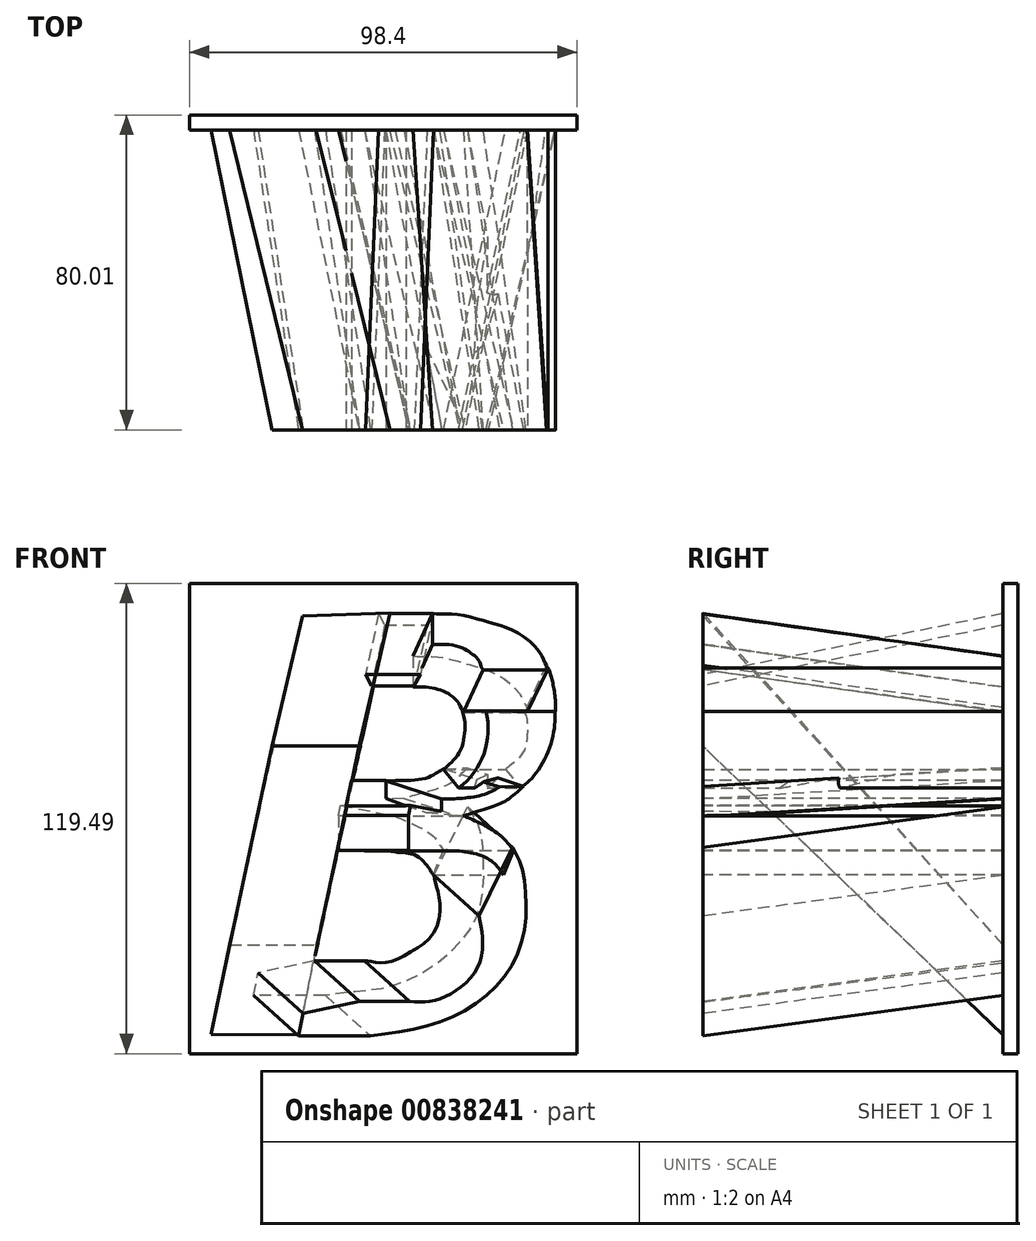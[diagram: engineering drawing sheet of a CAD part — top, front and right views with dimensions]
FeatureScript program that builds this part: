
annotation { "Feature Type Name" : "Feature", "Feature Type Description" : "" }
export const myFeature = defineFeature(function(context is Context, id is Id, definition is map)
    precondition{}
    {
        {
            var Q0;
            Q0=qCreatedBy(makeId("Front.planeOp"),FACE);
            var sketch = newSketch(context, id + "F0", { "sketchPlane" : qUnion([Q0])});
            skText(sketch, "E0", { "text": "B 3 D", "fontName": "OpenSans-BoldItalic.ttf"});
            const initialGuessF0  = {"E0": [-0.06398, -0.05174, 1, 0, 0.10807]};
            skSetInitialGuess(sketch, initialGuessF0);
            skSolve(sketch);
        }
        {
            var Q0;
            Q0 = qSketchRegion(id + "F0", true);
            var sketch = newSketch(context, id + "F1", { "sketchPlane" : qUnion([Q0])});
            skLineSegment(sketch, "E1", {"start": v(-36.57, 54.73) * mm, "end": v(-44.32, 21.63) * mm});
            skLineSegment(sketch, "E2", {"start": v(-44.32, 21.63) * mm, "end": v(-22.25, 21.63) * mm});
            skLineSegment(sketch, "E3", {"start": v(-22.25, 21.63) * mm, "end": v(-14.38, 55.5) * mm});
            skLineSegment(sketch, "E4", {"start": v(-14.38, 55.5) * mm, "end": v(-36.57, 54.73) * mm});
            skSolve(sketch);
        }
        {
            var Q0;
            Q0=qCreatedBy(makeId("Front.planeOp"),FACE);
            cPlane(context, id + "F2", {"entities" : qUnion([Q0]), "cplaneType" : CPlaneType.OFFSET, "offset" : 76.2 * mm, "oppositeDirection" : true, "width" : 152.4 * mm, "height" : 152.4 * mm});
        }
        {
            var Q0;
            Q0=qCreatedBy(id+"F2.planeOp",FACE);
            var sketch = newSketch(context, id + "F3", { "sketchPlane" : qUnion([Q0])});
            skLineSegment(sketch, "E5", {"start": v(-59.85, -51.56) * mm, "end": v(-55.1, -28.85) * mm});
            skLineSegment(sketch, "E6", {"start": v(-55.1, -28.85) * mm, "end": v(-33.1, -28.85) * mm});
            skLineSegment(sketch, "E7", {"start": v(-33.1, -28.85) * mm, "end": v(-37.58, -51.71) * mm});
            skLineSegment(sketch, "E8", {"start": v(-37.58, -51.71) * mm, "end": v(-59.85, -51.56) * mm});
            skSolve(sketch);
        }
        {
            var Q0;
            Q0 = qSketchRegion(id + "F3", true);
            var Q1;
            Q1 = qSketchRegion(id + "F1", true);
            loft(context, id + "F4", {"sheetProfilesArray" : [{ "sheetProfileEntities" : qUnion([Q0]) }, { "sheetProfileEntities" : qUnion([Q1]) }]});
        }
        {
            var Q0;
            Q0=qCreatedBy(id+"F2.planeOp",FACE);
            var sketch = newSketch(context, id + "F5", { "sketchPlane" : qUnion([Q0])});
            skPoint(sketch, "E9.0", {"position": v(-8.5, 41.11) * mm});
            skLineSegment(sketch, "E10.0", {"start": v(-8.5, 44.52) * mm, "end": v(-8.5, 37.7) * mm});
            skFitSpline(sketch, "E11.0", {"points": [v(-8.5, 44.52) * mm, v(-6.27, 44.45) * mm, v(-1.94, 44.3) * mm, v(3.93, 42.89) * mm, v(8.56, 41.52) * mm, v(13.4, 39.47) * mm, v(18.47, 35.08) * mm, v(19.84, 32.53) * mm, v(20.44, 31.4) * mm]});
            skFitSpline(sketch, "E12", {"points": [v(-8.5, 36.68) * mm, v(-4.4, 36.53) * mm, v(-1.12, 35.75) * mm, v(0.47, 35) * mm, v(1.65, 34.16) * mm, v(2.84, 32.92) * mm, v(4.25, 30.24) * mm], "startDerivative": vector(19.25, 0.13) * mm, "endDerivative": vector(7.37, -16.06) * mm});
            skLineSegment(sketch, "E13", {"start": v(4.25, 30.24) * mm, "end": v(20.71, 30.24) * mm});
            skLineSegment(sketch, "E14", {"start": v(20.71, 30.24) * mm, "end": v(20.44, 31.4) * mm});
            skLineSegment(sketch, "E15", {"start": v(-8.5, 37.7) * mm, "end": v(-8.5, 36.68) * mm});
            skSolve(sketch);
        }
        {
            var Q0;
            Q0=qCreatedBy(makeId("Front.planeOp"),FACE);
            var sketch = newSketch(context, id + "F6", { "sketchPlane" : qUnion([Q0])});
            skFitSpline(sketch, "E16.0", {"points": [v(-3.51, 55.29) * mm, v(-1.3, 55.21) * mm, v(3.03, 55.07) * mm, v(8.91, 53.66) * mm, v(13.54, 52.29) * mm, v(18.37, 50.24) * mm, v(23.45, 45.85) * mm, v(24.82, 43.3) * mm, v(25.42, 42.17) * mm]});
            skLineSegment(sketch, "E17.0", {"start": v(-3.51, 55.29) * mm, "end": v(-3.51, 48.47) * mm});
            skLineSegment(sketch, "E18.0", {"start": v(9.23, 41) * mm, "end": v(25.7, 41) * mm});
            skLineSegment(sketch, "E19.0", {"start": v(25.7, 41) * mm, "end": v(25.42, 42.17) * mm});
            skFitSpline(sketch, "E20.0", {"points": [v(-3.51, 47.44) * mm, v(-2.14, 47.45) * mm, v(0.48, 47.47) * mm, v(3.82, 46.63) * mm, v(5.44, 45.8) * mm, v(6.67, 44.94) * mm, v(7.98, 43.73) * mm, v(8.78, 42) * mm, v(9.23, 41) * mm]});
            skPoint(sketch, "E21.0", {"position": v(-3.51, 47.96) * mm});
            skLineSegment(sketch, "E22.0", {"start": v(-3.51, 48.47) * mm, "end": v(-3.51, 47.44) * mm});
            skSolve(sketch);
        }
        {
            var Q0;
            Q0 = qSketchRegion(id + "F5", true);
            var Q1;
            Q1 = qSketchRegion(id + "F6", true);
            loft(context, id + "F7", {"sheetProfilesArray" : [{ "sheetProfileEntities" : qUnion([Q0]) }, { "sheetProfileEntities" : qUnion([Q1]) }]});
        }
        {
            var Q0;
            Q0=qCreatedBy(makeId("Front.planeOp"),FACE);
            var sketch = newSketch(context, id + "F8", { "sketchPlane" : qUnion([Q0])});
            skLineSegment(sketch, "E23", {"start": v(-19, 36.93) * mm, "end": v(-8.22, 36.93) * mm});
            skLineSegment(sketch, "E24", {"start": v(-8.22, 36.93) * mm, "end": v(-6.62, 39.83) * mm});
            skLineSegment(sketch, "E25", {"start": v(-6.62, 39.83) * mm, "end": v(-20.55, 39.83) * mm});
            skLineSegment(sketch, "E26", {"start": v(-20.55, 39.83) * mm, "end": v(-19, 36.93) * mm});
            skSolve(sketch);
        }
        {
            var Q0;
            Q0=qCreatedBy(id+"F2.planeOp",FACE);
            var sketch = newSketch(context, id + "F9", { "sketchPlane" : qUnion([Q0])});
            skLineSegment(sketch, "E27.0", {"start": v(-3.32, 55.3) * mm, "end": v(-17.25, 55.3) * mm});
            skLineSegment(sketch, "E28.0", {"start": v(-4.92, 52.4) * mm, "end": v(-3.32, 55.3) * mm});
            skLineSegment(sketch, "E29.0", {"start": v(-15.7, 52.4) * mm, "end": v(-4.92, 52.4) * mm});
            skLineSegment(sketch, "E30.0", {"start": v(-17.25, 55.3) * mm, "end": v(-15.7, 52.4) * mm});
            skSolve(sketch);
        }
        {
            var Q0;
            Q0 = qSketchRegion(id + "F9", true);
            var Q1;
            Q1 = qSketchRegion(id + "F8", true);
            loft(context, id + "F10", {"sheetProfilesArray" : [{ "sheetProfileEntities" : qUnion([Q0]) }, { "sheetProfileEntities" : qUnion([Q1]) }]});
        }
        {
            var Q0;
            Q0=qCreatedBy(makeId("Front.planeOp"),FACE);
            var sketch = newSketch(context, id + "F11", { "sketchPlane" : qUnion([Q0])});
            skFitSpline(sketch, "E31", {"points": [v(4.05, 30.54) * mm, v(4.56, 28.47) * mm, v(4.67, 25.83) * mm, v(3.79, 21.17) * mm, v(1.56, 17.8) * mm, v(-0.77, 15.73) * mm], "startDerivative": vector(3.71, -12.67) * mm, "endDerivative": vector(-12.07, -9.82) * mm});
            skLineSegment(sketch, "E32", {"start": v(4.05, 30.54) * mm, "end": v(10.06, 30.54) * mm});
            skArc(sketch, "E33", {"start": v(3.06, 10.96) * mm, "mid": v(9.5, 19.7) * mm, "end": v(10.06, 30.54) * mm});
            skLineSegment(sketch, "E34", {"start": v(-0.77, 15.73) * mm, "end": v(3.06, 10.96) * mm});
            skSolve(sketch);
        }
        {
            var Q0;
            Q0=qCreatedBy(id+"F2.planeOp",FACE);
            var sketch = newSketch(context, id + "F12", { "sketchPlane" : qUnion([Q0])});
            skFitSpline(sketch, "E35.0", {"points": [v(19.8, 30.54) * mm, v(20, 29.86) * mm, v(20.42, 28.42) * mm, v(20.51, 25.77) * mm, v(19.9, 21) * mm, v(17.44, 17.73) * mm, v(15.76, 16.37) * mm, v(14.98, 15.73) * mm]});
            skLineSegment(sketch, "E36.0", {"start": v(19.8, 30.54) * mm, "end": v(27.6, 30.36) * mm});
            skLineSegment(sketch, "E37.0", {"start": v(14.98, 15.73) * mm, "end": v(18.81, 10.96) * mm});
            skFitSpline(sketch, "E38", {"points": [v(18.81, 10.96) * mm, v(21.53, 13.35) * mm, v(25, 18.44) * mm, v(27.27, 25.48) * mm, v(27.6, 30.36) * mm], "startDerivative": vector(13.19, 10.31) * mm, "endDerivative": vector(0.16, 19.48) * mm});
            skSolve(sketch);
        }
        {
            var Q1;
            Q1 = qSketchRegion(id + "F11", true);
            var Q2;
            Q2 = qSketchRegion(id + "F12", true);
            loft(context, id + "F13", {"operationType" : NewBodyOperationType.ADD, "sheetProfilesArray" : [{ "sheetProfileEntities" : qUnion([Q1]) }, { "sheetProfileEntities" : qUnion([Q2]) }]});
        }
        {
            var Q0;
            Q0=qCreatedBy(makeId("Front.planeOp"),FACE);
            var sketch = newSketch(context, id + "F14", { "sketchPlane" : qUnion([Q0])});
            skLineSegment(sketch, "E39", {"start": v(20.54, 30.41) * mm, "end": v(25.82, 41.45) * mm});
            skLineSegment(sketch, "E40", {"start": v(20.54, 30.41) * mm, "end": v(27.69, 30.41) * mm});
            skFitSpline(sketch, "E41", {"points": [v(25.82, 41.45) * mm, v(26.6, 39.48) * mm, v(27.17, 36.78) * mm, v(27.64, 33.31) * mm, v(27.69, 30.41) * mm], "startDerivative": vector(3.88, -8.71) * mm, "endDerivative": vector(-0.15, -11.05) * mm});
            skSolve(sketch);
        }
        {
            var Q0;
            Q0 = qSketchRegion(id + "F14", true);
            var Q1;
            Q1=makeQuery(id+"F13.boolean.opBoolean","MERGE",FACE,{"derivedFrom":[makeQuery(id+"F7.opLoft","CAP_FACE",FACE,{"disambiguationData":[OSD([makeQuery(id+"F5.imprint","IMPRINT",FACE,{"disambiguationData":[TD([[makeQuery(id+"F5.imprint","IMPRINT",EDGE,{"derivedFrom":sQuery(id+"F5.wireOp",EDGE,"E10.0")}),1.0]])]})])],"isStart":true}),makeQuery(id+"F13.opLoft","CAP_FACE",FACE,{"disambiguationData":[OSD([makeQuery(id+"F12.imprint","IMPRINT",FACE,{"disambiguationData":[TD([[makeQuery(id+"F12.imprint","IMPRINT",EDGE,{"derivedFrom":sQuery(id+"F12.wireOp",EDGE,"E35.0")}),1.0]])]})])],"isStart":true})]});
            extrude(context, id + "F15", {"entities" : qUnion([Q0]), "operationType" : NewBodyOperationType.ADD, "endBound" : BoundingType.UP_TO_SURFACE, "oppositeDirection" : true, "depth" : 25.4 * mm, "endBoundEntityFace" : qUnion([Q1]), "offsetDistance" : 25.4 * mm});
        }
        {
            var Q0;
            Q0=qCreatedBy(makeId("Front.planeOp"),FACE);
            var sketch = newSketch(context, id + "F16", { "sketchPlane" : qUnion([Q0])});
            skFitSpline(sketch, "E42", {"points": [v(19.51, 11.44) * mm, v(15.76, 8.19) * mm, v(11.61, 6.21) * mm, v(3.42, 3.74) * mm], "startDerivative": vector(-12.15, -11.7) * mm, "endDerivative": vector(-22.23, -6.28) * mm});
            skFitSpline(sketch, "E43", {"points": [v(13.5, 11.25) * mm, v(9.52, 9.37) * mm, v(3.89, 8.38) * mm, v(-1.25, 8.19) * mm], "startDerivative": vector(-12.02, -6.71) * mm, "endDerivative": vector(-14.93, -0.24) * mm});
            skLineSegment(sketch, "E44", {"start": v(-1.25, 8.19) * mm, "end": v(-1.25, 3.54) * mm});
            skLineSegment(sketch, "E45", {"start": v(3.42, 3.74) * mm, "end": v(-1.25, 3.54) * mm});
            skLineSegment(sketch, "E46", {"start": v(13.5, 11.25) * mm, "end": v(19.51, 11.44) * mm});
            skSolve(sketch);
        }
        {
            var Q0;
            Q0=qCreatedBy(id+"F2.planeOp",FACE);
            var sketch = newSketch(context, id + "F17", { "sketchPlane" : qUnion([Q0])});
            skFitSpline(sketch, "E47.0", {"points": [v(-0.72, 15.89) * mm, v(-1.96, 15.2) * mm, v(-4.63, 13.7) * mm, v(-10.37, 12.9) * mm, v(-13.8, 12.85) * mm, v(-15.47, 12.83) * mm]});
            skFitSpline(sketch, "E48.0", {"points": [v(5.29, 16.08) * mm, v(4.05, 14.9) * mm, v(1.62, 12.56) * mm, v(-2.69, 10.68) * mm, v(-7.84, 9.22) * mm, v(-10.8, 8.38) * mm]});
            skLineSegment(sketch, "E49.0", {"start": v(-0.72, 15.89) * mm, "end": v(5.29, 16.08) * mm});
            skPoint(sketch, "E50.0", {"position": v(-15.47, 10.5) * mm});
            skLineSegment(sketch, "E51.0", {"start": v(-15.47, 12.83) * mm, "end": v(-15.47, 8.19) * mm});
            skLineSegment(sketch, "E52.0", {"start": v(-10.8, 8.38) * mm, "end": v(-15.47, 8.19) * mm});
            skSolve(sketch);
        }
        {
            var Q1;
            Q1 = qSketchRegion(id + "F17", true);
            var Q2;
            Q2 = qSketchRegion(id + "F16", true);
            loft(context, id + "F18", {"operationType" : NewBodyOperationType.ADD, "sheetProfilesArray" : [{ "sheetProfileEntities" : qUnion([Q1]) }, { "sheetProfileEntities" : qUnion([Q2]) }]});
        }
        {
            var Q0;
            Q0=qCreatedBy(makeId("Front.planeOp"),FACE);
            var sketch = newSketch(context, id + "F19", { "sketchPlane" : qUnion([Q0])});
            skLineSegment(sketch, "E53", {"start": v(-9.63, 4) * mm, "end": v(-9.12, 6.6) * mm});
            skLineSegment(sketch, "E54", {"start": v(-9.12, 6.6) * mm, "end": v(4.64, 3.85) * mm});
            skFitSpline(sketch, "E55", {"points": [v(4.64, 3.85) * mm, v(10.03, 1.29) * mm, v(14.31, -1.61) * mm, v(16.96, -4.8) * mm], "startDerivative": vector(15.2, -6.8) * mm, "endDerivative": vector(7.92, -10.99) * mm});
            skLineSegment(sketch, "E56", {"start": v(-3.1, -4.96) * mm, "end": v(3.3, -4.96) * mm});
            skFitSpline(sketch, "E57", {"points": [v(3.3, -4.96) * mm, v(9.66, -6.5) * mm, v(12.76, -8.84) * mm, v(14.45, -11.15) * mm], "startDerivative": vector(16.9, -2.74) * mm, "endDerivative": vector(5.65, -8.57) * mm});
            skLineSegment(sketch, "E58", {"start": v(-9.63, 4) * mm, "end": v(-9.63, -4.88) * mm});
            skLineSegment(sketch, "E59", {"start": v(-9.63, -4.88) * mm, "end": v(-3.1, -4.96) * mm});
            skLineSegment(sketch, "E60", {"start": v(14.45, -11.15) * mm, "end": v(16.96, -4.8) * mm});
            skSolve(sketch);
        }
        {
            var Q0;
            Q0=qCreatedBy(id+"F2.planeOp",FACE);
            var sketch = newSketch(context, id + "F20", { "sketchPlane" : qUnion([Q0])});
            skPoint(sketch, "E61.0", {"position": v(-27.15, 5.3) * mm});
            skFitSpline(sketch, "E62.0", {"points": [v(-14.49, -4.96) * mm, v(-12.17, -5.34) * mm, v(-8.07, -6) * mm, v(-4.95, -8.69) * mm, v(-3.84, -10.37) * mm, v(-3.33, -11.15) * mm]});
            skLineSegment(sketch, "E63.0", {"start": v(-20.88, -4.96) * mm, "end": v(-14.49, -4.96) * mm});
            skLineSegment(sketch, "E64.0", {"start": v(-27.41, -4.88) * mm, "end": v(-20.88, -4.96) * mm});
            skLineSegment(sketch, "E65.0", {"start": v(-27.41, 4) * mm, "end": v(-27.41, -4.88) * mm});
            skLineSegment(sketch, "E66.0", {"start": v(-27.41, 4) * mm, "end": v(-26.9, 6.6) * mm});
            skLineSegment(sketch, "E67.0", {"start": v(-26.9, 6.6) * mm, "end": v(-13.14, 3.85) * mm});
            skFitSpline(sketch, "E68.0", {"points": [v(-13.14, 3.85) * mm, v(-11.3, 3.03) * mm, v(-7.76, 1.44) * mm, v(-3.3, -1.36) * mm, v(-1.62, -3.7) * mm, v(-0.82, -4.8) * mm]});
            skLineSegment(sketch, "E69.0", {"start": v(-3.33, -11.15) * mm, "end": v(-0.82, -4.8) * mm});
            skSolve(sketch);
        }
        {
            var Q1;
            Q1 = qSketchRegion(id + "F20", true);
            var Q2;
            Q2 = qSketchRegion(id + "F19", true);
            loft(context, id + "F21", {"operationType" : NewBodyOperationType.ADD, "sheetProfilesArray" : [{ "sheetProfileEntities" : qUnion([Q1]) }, { "sheetProfileEntities" : qUnion([Q2]) }]});
        }
        {
            var Q0;
            Q0=qCreatedBy(makeId("Front.planeOp"),FACE);
            var sketch = newSketch(context, id + "F22", { "sketchPlane" : qUnion([Q0])});
            skLineSegment(sketch, "E70", {"start": v(-24.15, 12.97) * mm, "end": v(-15.4, 12.97) * mm});
            skLineSegment(sketch, "E71", {"start": v(-15.4, 12.97) * mm, "end": v(-15.4, 8.4) * mm});
            skLineSegment(sketch, "E72", {"start": v(-15.4, 8.4) * mm, "end": v(-10.3, 6.47) * mm});
            skLineSegment(sketch, "E73", {"start": v(-10.3, 6.47) * mm, "end": v(-25.57, 6.47) * mm});
            skLineSegment(sketch, "E74", {"start": v(-25.57, 6.47) * mm, "end": v(-24.15, 12.97) * mm});
            skSolve(sketch);
        }
        {
            var Q0;
            Q0 = qSketchRegion(id + "F22", true);
            var Q1;
            {var subQ0=makeQuery(id+"F12.imprint","IMPRINT",FACE,{"disambiguationData":[TD([[makeQuery(id+"F12.imprint","IMPRINT",EDGE,{"derivedFrom":sQuery(id+"F12.wireOp",EDGE,"E35.0")}),1.0]])]});var subQ1=makeQuery(id+"F5.imprint","IMPRINT",FACE,{"disambiguationData":[TD([[makeQuery(id+"F5.imprint","IMPRINT",EDGE,{"derivedFrom":sQuery(id+"F5.wireOp",EDGE,"E10.0")}),1.0]])]});Q1=makeQuery(id+"F15.boolean.opBoolean","MERGE",FACE,{"derivedFrom":[makeQuery(id+"F13.boolean.opBoolean","MERGE",FACE,{"derivedFrom":[makeQuery(id+"F7.opLoft","CAP_FACE",FACE,{"disambiguationData":[OSD([subQ1])],"isStart":true}),makeQuery(id+"F13.opLoft","CAP_FACE",FACE,{"disambiguationData":[OSD([subQ0])],"isStart":true})]}),makeQuery(id+"F15.opExtrude","CAP_FACE",FACE,{"disambiguationData":[OSD([subQ1,subQ0])],"isStart":false})]});}
            extrude(context, id + "F23", {"entities" : qUnion([Q0]), "endBound" : BoundingType.UP_TO_SURFACE, "oppositeDirection" : true, "depth" : 25.4 * mm, "endBoundEntityFace" : qUnion([Q1]), "offsetDistance" : 25.4 * mm});
        }
        {
            var Q0;
            Q0=qCreatedBy(makeId("Front.planeOp"),FACE);
            var sketch = newSketch(context, id + "F24", { "sketchPlane" : qUnion([Q0])});
            skFitSpline(sketch, "E75", {"points": [v(16.73, -4.1) * mm, v(18.93, -8.64) * mm, v(20.24, -19.19) * mm, v(17.9, -31.5) * mm, v(9.55, -42.19) * mm, v(-3.2, -48.93) * mm, v(-19.31, -52) * mm], "startDerivative": vector(21.9, -36.48) * mm, "endDerivative": vector(-84.3, -11.37) * mm});
            skLineSegment(sketch, "E76", {"start": v(-19.31, -52) * mm, "end": v(-37.62, -52) * mm});
            skLineSegment(sketch, "E77", {"start": v(-37.62, -52) * mm, "end": v(-36.45, -46.3) * mm});
            skLineSegment(sketch, "E78", {"start": v(-22.14, -43.23) * mm, "end": v(-9.39, -43.23) * mm});
            skFitSpline(sketch, "E79", {"points": [v(-9.39, -43.23) * mm, v(-4.25, -43.23) * mm, v(1.91, -40.76) * mm, v(7.64, -35.1) * mm, v(9.18, -27.58) * mm, v(8.2, -21.54) * mm], "startDerivative": vector(28.88, -2.42) * mm, "endDerivative": vector(-7.1, 30.22) * mm});
            skLineSegment(sketch, "E80", {"start": v(8.2, -21.54) * mm, "end": v(16.73, -4.1) * mm});
            skLineSegment(sketch, "E81", {"start": v(-22.14, -43.23) * mm, "end": v(-36.45, -46.3) * mm});
            skSolve(sketch);
        }
        {
            var Q0;
            Q0=qCreatedBy(id+"F2.planeOp",FACE);
            var sketch = newSketch(context, id + "F25", { "sketchPlane" : qUnion([Q0])});
            skLineSegment(sketch, "E82.0", {"start": v(-49.05, -41.7) * mm, "end": v(-47.88, -35.99) * mm});
            skLineSegment(sketch, "E83.0", {"start": v(-30.74, -41.7) * mm, "end": v(-49.05, -41.7) * mm});
            skFitSpline(sketch, "E84.0", {"points": [v(5.3, 6.2) * mm, v(6.1, 4.88) * mm, v(8.05, 1.62) * mm, v(9.35, -9.25) * mm, v(7.56, -21.67) * mm, v(-1.38, -32.77) * mm, v(-14.5, -39.51) * mm, v(-25.21, -40.96) * mm, v(-30.74, -41.7) * mm]});
            skLineSegment(sketch, "E85.0", {"start": v(-3.23, -11.24) * mm, "end": v(5.3, 6.2) * mm});
            skFitSpline(sketch, "E86.0", {"points": [v(-20.82, -32.93) * mm, v(-19.13, -33.07) * mm, v(-15.52, -33.37) * mm, v(-9.25, -30.78) * mm, v(-2.93, -25.31) * mm, v(-1.82, -17.26) * mm, v(-2.78, -13.17) * mm, v(-3.23, -11.24) * mm]});
            skLineSegment(sketch, "E87.0", {"start": v(-33.57, -32.93) * mm, "end": v(-20.82, -32.93) * mm});
            skLineSegment(sketch, "E88.0", {"start": v(-33.57, -32.93) * mm, "end": v(-47.88, -35.99) * mm});
            skSolve(sketch);
        }
        {
            var Q0;
            Q0 = qSketchRegion(id + "F25", true);
            var Q1;
            Q1 = qSketchRegion(id + "F24", true);
            loft(context, id + "F26", {"sheetProfilesArray" : [{ "sheetProfileEntities" : qUnion([Q0]) }, { "sheetProfileEntities" : qUnion([Q1]) }]});
        }
        {
            var Q0;
            Q0=qCreatedBy(id+"F2.planeOp",FACE);
            var sketch = newSketch(context, id + "F27", { "sketchPlane" : qUnion([Q0])});
            skLineSegment(sketch, "E89.bottom", {"start": v(33.13, 63) * mm, "end": v(-65.27, 63) * mm});
            skLineSegment(sketch, "E89.top", {"start": v(33.13, -56.5) * mm, "end": v(-65.27, -56.5) * mm});
            skLineSegment(sketch, "E89.left", {"start": v(33.13, 63) * mm, "end": v(33.13, -56.5) * mm});
            skLineSegment(sketch, "E89.right", {"start": v(-65.27, 63) * mm, "end": v(-65.27, -56.5) * mm});
            skSolve(sketch);
        }
        {
            var Q0;
            Q0=makeQuery(id+"F27.imprint","IMPRINT",FACE,{"disambiguationData":[TD([[makeQuery(id+"F27.imprint","IMPRINT",EDGE,{"derivedFrom":sQuery(id+"F27.wireOp",EDGE,"E89.bottom")}),1.0]])]});
            extrude(context, id + "F28", {"entities" : qUnion([Q0]), "oppositeDirection" : true, "depth" : 3.8 * mm, "offsetDistance" : 25.4 * mm});
        }
    });
